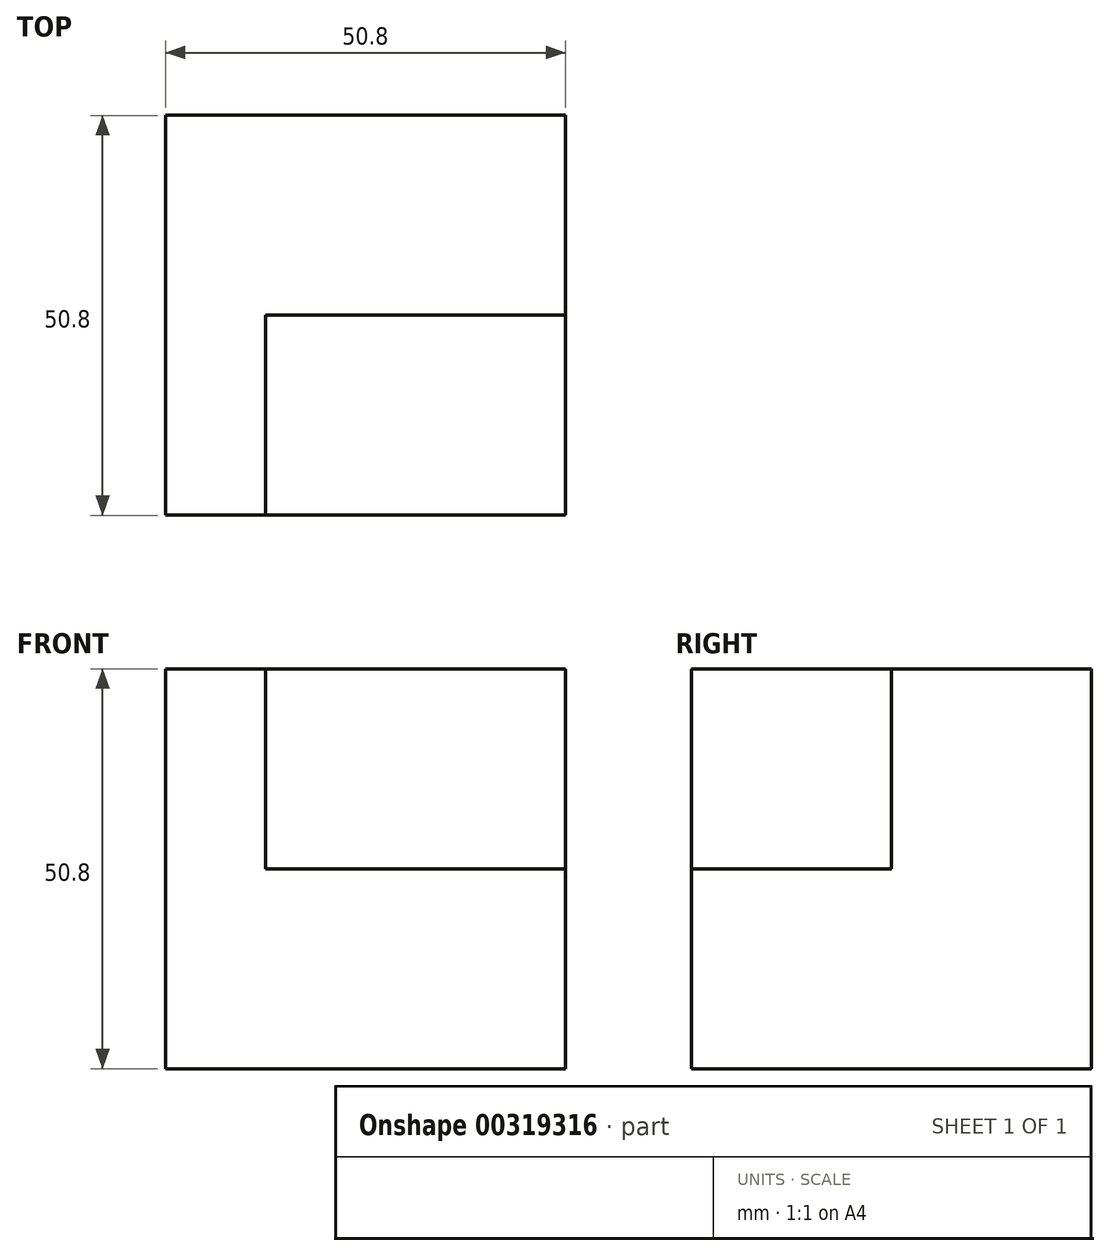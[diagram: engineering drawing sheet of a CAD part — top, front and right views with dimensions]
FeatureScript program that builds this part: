
annotation { "Feature Type Name" : "Feature", "Feature Type Description" : "" }
export const myFeature = defineFeature(function(context is Context, id is Id, definition is map)
    precondition{}
    {
        {
            var Q0;
            Q0=qCreatedBy(makeId("Top.planeOp"),FACE);
            var sketch = newSketch(context, id + "F0", { "sketchPlane" : qUnion([Q0])});
            skLineSegment(sketch, "E0", {"start": v(-19.2, -18.75) * mm, "end": v(31.6, -18.75) * mm});
            skLineSegment(sketch, "E1", {"start": v(31.6, -18.75) * mm, "end": v(31.6, 32.05) * mm});
            skLineSegment(sketch, "E2", {"start": v(31.6, 32.05) * mm, "end": v(-19.2, 32.05) * mm});
            skLineSegment(sketch, "E3", {"start": v(-19.2, 32.05) * mm, "end": v(-19.2, -18.75) * mm});
            skSolve(sketch);
        }
        {
            var Q0;
            Q0=makeQuery(id+"F0.imprint","IMPRINT",FACE,{"disambiguationData":[TD([[makeQuery(id+"F0.imprint","IMPRINT",EDGE,{"derivedFrom":sQuery(id+"F0.wireOp",EDGE,"E0")}),1.0]])]});
            extrude(context, id + "F1", {"entities" : qUnion([Q0]), "depth" : 25.4 * mm});
        }
        {
            var Q0;
            Q0=makeQuery(id+"F1.opExtrude","CAP_FACE",FACE,{"disambiguationData":[OSD([sQuery(id+"F0.wireOp",EDGE,"E0"),sQuery(id+"F0.wireOp",EDGE,"E1"),sQuery(id+"F0.wireOp",EDGE,"E2"),sQuery(id+"F0.wireOp",EDGE,"E3")])],"isStart":false});
            var sketch = newSketch(context, id + "F2", { "sketchPlane" : qUnion([Q0])});
            skLineSegment(sketch, "E4", {"start": v(-19.2, -18.75) * mm, "end": v(-6.5, -18.75) * mm});
            skLineSegment(sketch, "E5", {"start": v(-6.5, -18.75) * mm, "end": v(-6.5, 6.65) * mm});
            skLineSegment(sketch, "E6", {"start": v(-6.5, 6.65) * mm, "end": v(31.6, 6.65) * mm});
            skPoint(sketch, "E6.endSnap0", {"position": v(31.6, 6.65) * mm});
            skLineSegment(sketch, "E7", {"start": v(31.6, 6.65) * mm, "end": v(31.6, 32.05) * mm});
            skLineSegment(sketch, "E8", {"start": v(31.6, 32.05) * mm, "end": v(-19.2, 32.05) * mm});
            skLineSegment(sketch, "E9", {"start": v(-19.2, 32.05) * mm, "end": v(-19.2, -18.75) * mm});
            skSolve(sketch);
        }
        {
            var Q0;
            Q0=makeQuery(id+"F2.imprint","IMPRINT",FACE,{"disambiguationData":[TD([[makeQuery(id+"F2.imprint","IMPRINT",EDGE,{"derivedFrom":sQuery(id+"F2.wireOp",EDGE,"E4")}),1.0]])]});
            extrude(context, id + "F3", {"entities" : qUnion([Q0]), "operationType" : NewBodyOperationType.ADD, "depth" : 25.4 * mm});
        }
    });
